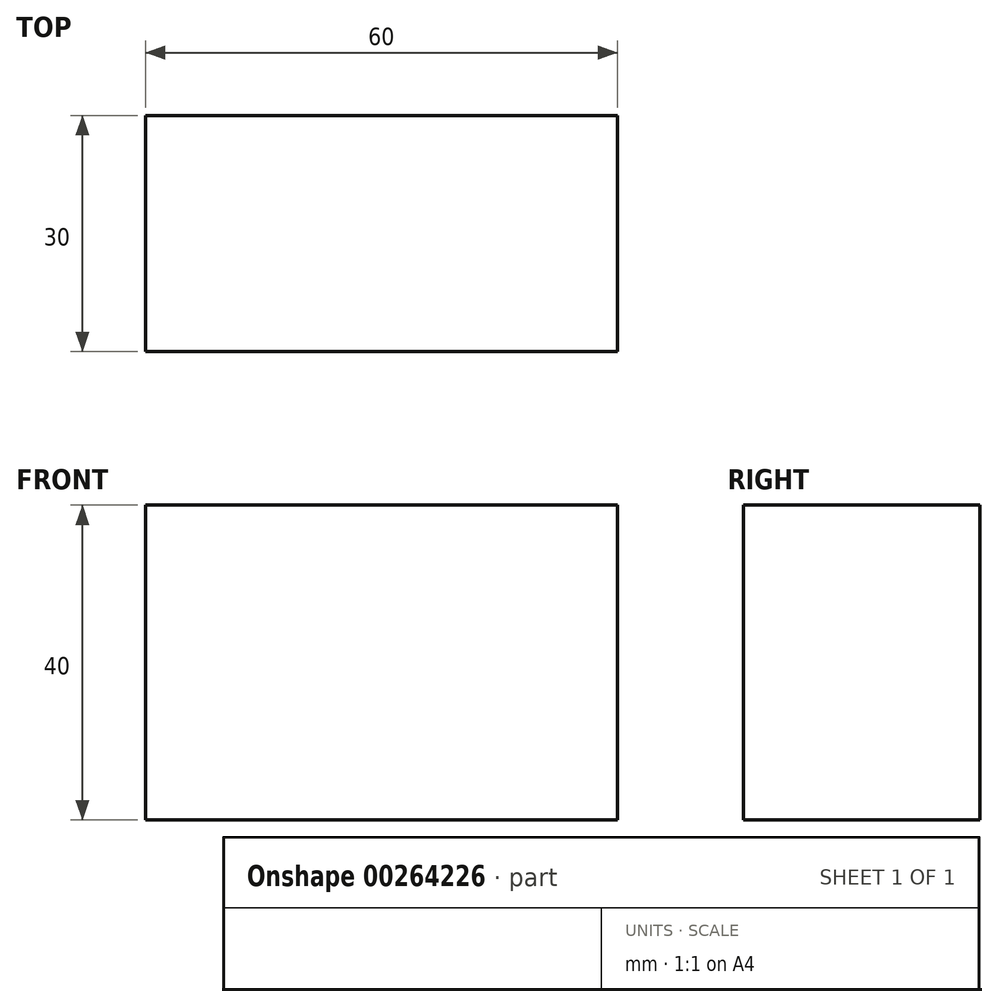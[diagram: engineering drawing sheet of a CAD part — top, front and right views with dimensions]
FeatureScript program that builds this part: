
annotation { "Feature Type Name" : "Feature", "Feature Type Description" : "" }
export const myFeature = defineFeature(function(context is Context, id is Id, definition is map)
    precondition{}
    {
        {
            var Q0;
            Q0=qCreatedBy(makeId("Front.planeOp"),FACE);
            var sketch = newSketch(context, id + "F0", { "sketchPlane" : qUnion([Q0])});
            skLineSegment(sketch, "E0.bottom", {"start": v(-30.3, 8.99) * mm, "end": v(29.7, 8.99) * mm});
            skLineSegment(sketch, "E0.top", {"start": v(-30.3, -31.01) * mm, "end": v(29.7, -31.01) * mm});
            skLineSegment(sketch, "E0.left", {"start": v(-30.3, 8.99) * mm, "end": v(-30.3, -31.01) * mm});
            skLineSegment(sketch, "E0.right", {"start": v(29.7, 8.99) * mm, "end": v(29.7, -31.01) * mm});
            skSolve(sketch);
        }
        {
            var Q0;
            Q0 = qSketchRegion(id + "F0", true);
            extrude(context, id + "F1", {"entities" : qUnion([Q0]), "depth" : 30 * mm});
        }
    });
